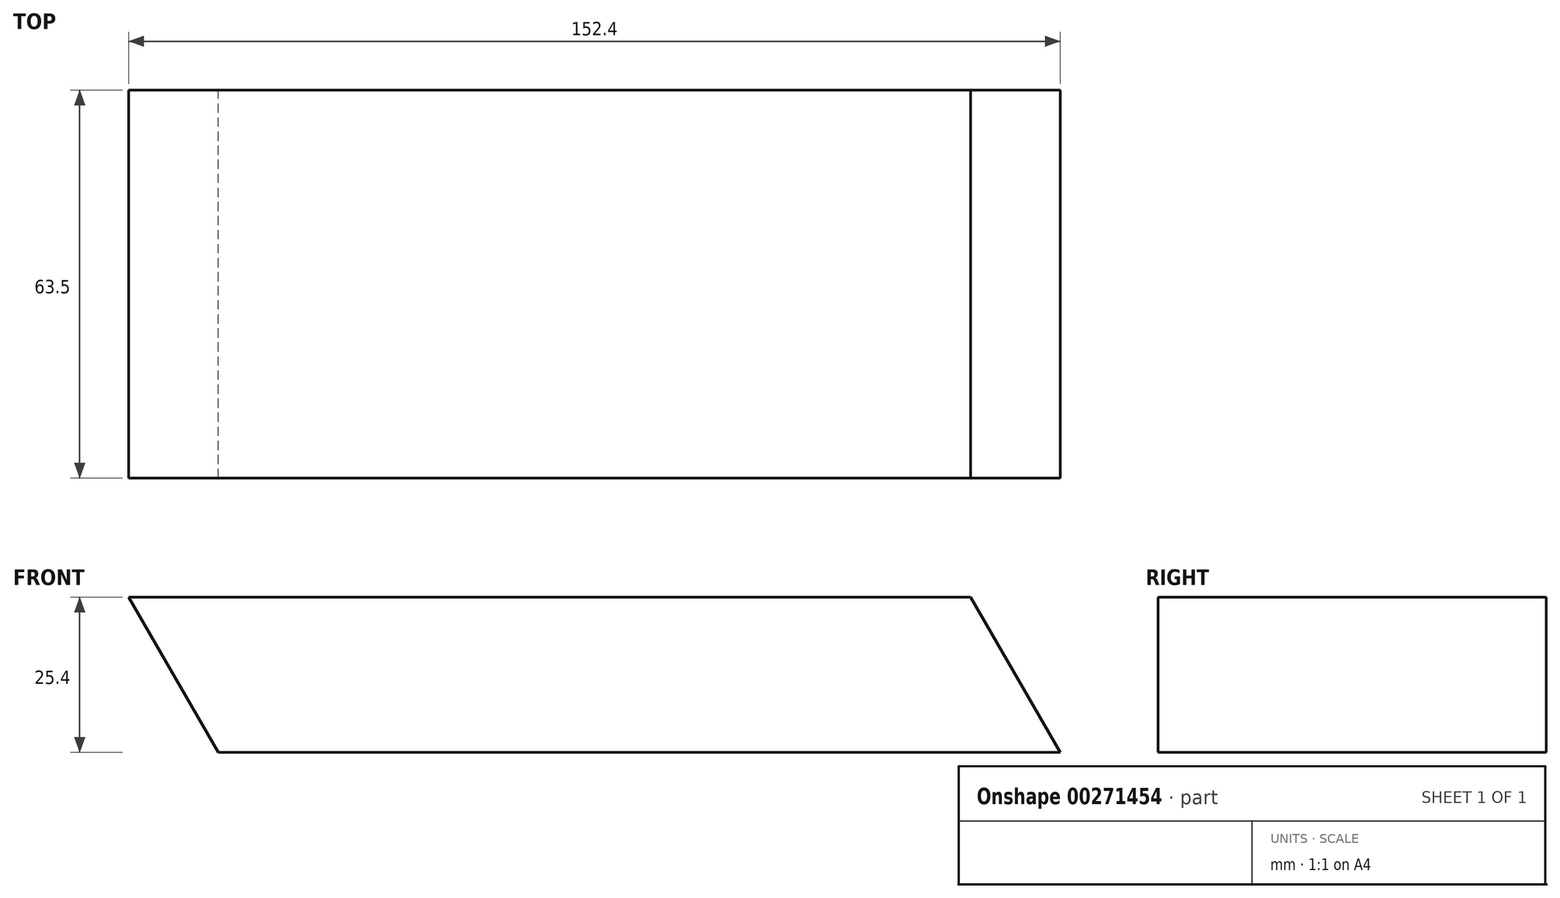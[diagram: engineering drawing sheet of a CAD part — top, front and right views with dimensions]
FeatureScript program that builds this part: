
annotation { "Feature Type Name" : "Feature", "Feature Type Description" : "" }
export const myFeature = defineFeature(function(context is Context, id is Id, definition is map)
    precondition{}
    {
        {
            var Q0;
            Q0=qCreatedBy(makeId("Top.planeOp"),FACE);
            var sketch = newSketch(context, id + "F0", { "sketchPlane" : qUnion([Q0])});
            skLineSegment(sketch, "E0.bottom", {"start": v(-67.34, 0) * mm, "end": v(85.06, 0) * mm});
            skLineSegment(sketch, "E0.top", {"start": v(-67.34, -63.5) * mm, "end": v(85.06, -63.5) * mm});
            skLineSegment(sketch, "E0.left", {"start": v(-67.34, 0) * mm, "end": v(-67.34, -63.5) * mm});
            skLineSegment(sketch, "E0.right", {"start": v(85.06, 0) * mm, "end": v(85.06, -63.5) * mm});
            skSolve(sketch);
        }
        {
            var Q0;
            Q0 = qSketchRegion(id + "F0", true);
            extrude(context, id + "F1", {"entities" : qUnion([Q0]), "depth" : 25.4 * mm});
        }
        {
            var Q0;
            Q0=makeQuery(id+"F1.opExtrude","CAP_EDGE",EDGE,{"disambiguationData":[OSD([sQuery(id+"F0.wireOp",EDGE,"E0.right")])],"isStart":false});
            chamfer(context, id + "F2", {"entities" : qUnion([Q0]), "chamferType" : ChamferType.OFFSET_ANGLE, "width" : 25.4 * mm, "oppositeDirection" : false, "angle" : 30 * degree, "tangentPropagation" : true});
        }
        {
            var Q0;
            Q0=makeQuery(id+"F1.opExtrude","CAP_EDGE",EDGE,{"disambiguationData":[OSD([sQuery(id+"F0.wireOp",EDGE,"E0.left")])],"isStart":true});
            chamfer(context, id + "F3", {"entities" : qUnion([Q0]), "chamferType" : ChamferType.OFFSET_ANGLE, "width" : 25.4 * mm, "oppositeDirection" : false, "angle" : 30 * degree, "tangentPropagation" : true});
        }
    });
